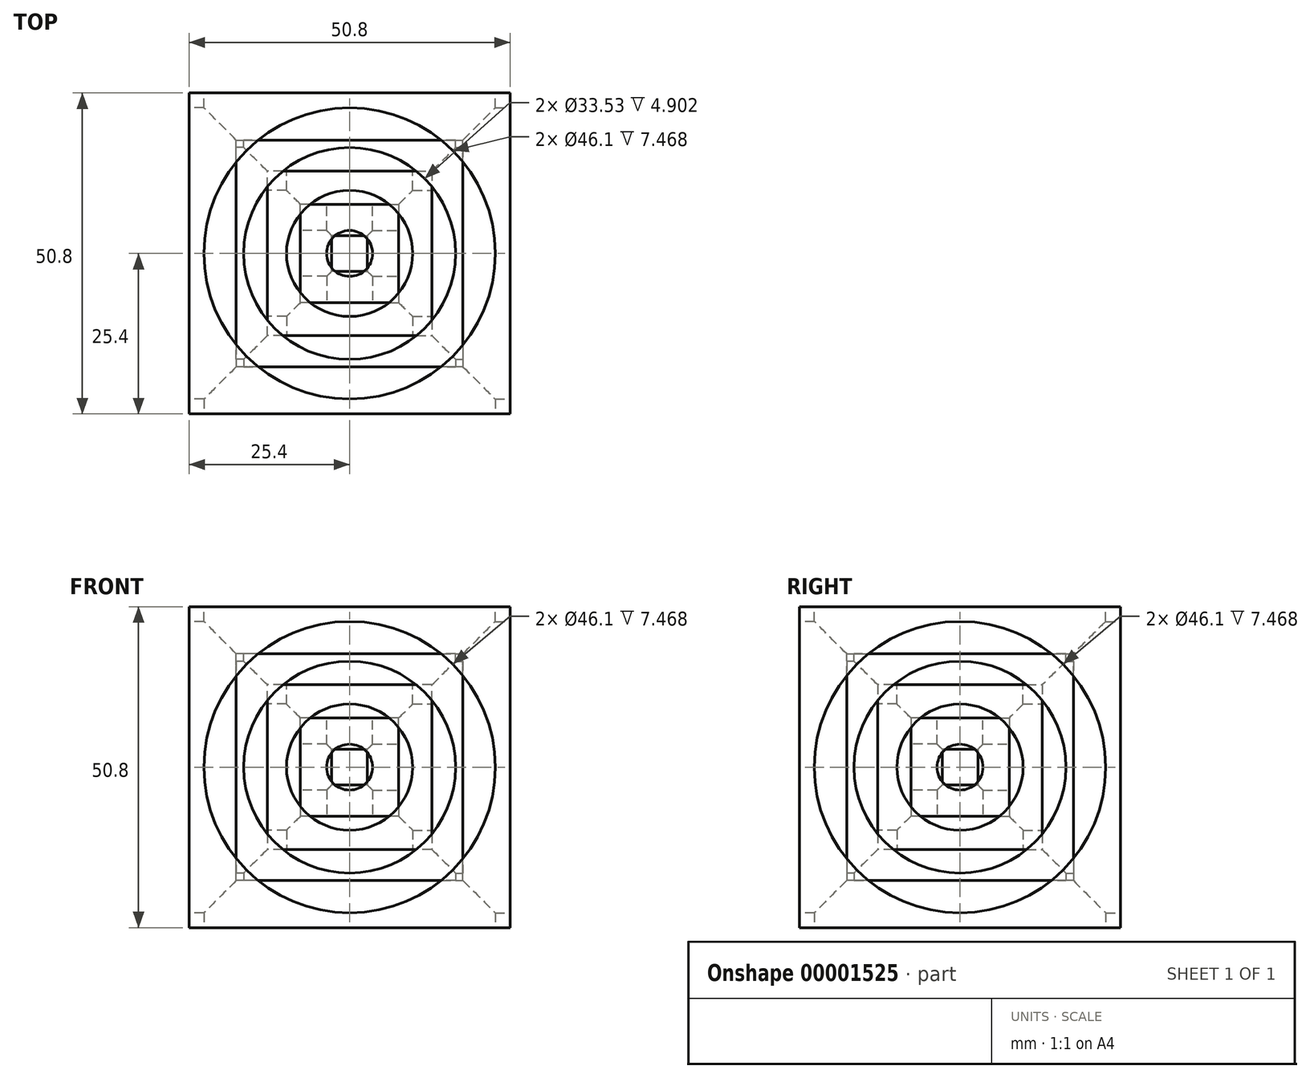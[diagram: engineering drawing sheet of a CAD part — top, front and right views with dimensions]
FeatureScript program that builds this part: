
annotation { "Feature Type Name" : "Feature", "Feature Type Description" : "" }
export const myFeature = defineFeature(function(context is Context, id is Id, definition is map)
    precondition{}
    {
        {
            var Q0;
            Q0=qCreatedBy(makeId("Top.planeOp"),FACE);
            var sketch = newSketch(context, id + "F0", { "sketchPlane" : qUnion([Q0])});
            skLineSegment(sketch, "E0.bottom", {"start": v(-25.4, 25.4) * mm, "end": v(25.4, 25.4) * mm});
            skLineSegment(sketch, "E0.top", {"start": v(-25.4, -25.4) * mm, "end": v(25.4, -25.4) * mm});
            skLineSegment(sketch, "E0.left", {"start": v(-25.4, 25.4) * mm, "end": v(-25.4, -25.4) * mm});
            skLineSegment(sketch, "E0.right", {"start": v(25.4, 25.4) * mm, "end": v(25.4, -25.4) * mm});
            skPoint(sketch, "E1", {"position": v(-25.4, 0) * mm});
            skPoint(sketch, "E2", {"position": v(0, 25.4) * mm});
            skSolve(sketch);
        }
        {
            var Q0;
            Q0 = qSketchRegion(id + "F0", true);
            extrude(context, id + "F1", {"entities" : qUnion([Q0]), "endBound" : BoundingType.SYMMETRIC, "oppositeDirection" : true, "depth" : 50.8 * mm});
        }
        {
            var Q0;
            Q0=qCreatedBy(makeId("Front.planeOp"),FACE);
            var sketch = newSketch(context, id + "F2", { "sketchPlane" : qUnion([Q0])});
            skLineSegment(sketch, "E3", {"start": v(23.05, 25.4) * mm, "end": v(23.05, 17.93) * mm});
            skLineSegment(sketch, "E4", {"start": v(23.05, 17.93) * mm, "end": v(16.76, 17.93) * mm});
            skLineSegment(sketch, "E5", {"start": v(16.76, 17.93) * mm, "end": v(16.76, 13.03) * mm});
            skLineSegment(sketch, "E6", {"start": v(16.76, 13.03) * mm, "end": v(9.98, 13.03) * mm});
            skLineSegment(sketch, "E7", {"start": v(9.98, 13.03) * mm, "end": v(9.98, 7.77) * mm});
            skLineSegment(sketch, "E8", {"start": v(9.98, 7.77) * mm, "end": v(3.63, 7.77) * mm});
            skLineSegment(sketch, "E9", {"start": v(3.63, 7.77) * mm, "end": v(3.63, 2.82) * mm});
            skLineSegment(sketch, "E10", {"start": v(3.63, 2.82) * mm, "end": v(0, 2.82) * mm});
            skLineSegment(sketch, "E11", {"start": v(0, 2.82) * mm, "end": v(0, 25.4) * mm});
            skLineSegment(sketch, "E12", {"start": v(0, 25.4) * mm, "end": v(23.05, 25.4) * mm});
            skLineSegment(sketch, "E13.0.MirrorCS", {"start": v(-23.05, 25.4) * mm, "end": v(-23.05, 17.93) * mm});
            skLineSegment(sketch, "E14.0.MirrorCS", {"start": v(-16.76, 17.93) * mm, "end": v(-16.76, 13.03) * mm});
            skLineSegment(sketch, "E15.0.MirrorCS", {"start": v(-9.98, 13.03) * mm, "end": v(-9.98, 7.77) * mm});
            skLineSegment(sketch, "E16.0.MirrorCS", {"start": v(-3.63, 7.77) * mm, "end": v(-3.63, 2.82) * mm});
            skLineSegment(sketch, "E17.0.MirrorCS", {"start": v(0, 25.4) * mm, "end": v(-23.05, 25.4) * mm});
            skLineSegment(sketch, "E18.0.MirrorCS", {"start": v(-23.05, 17.93) * mm, "end": v(-16.76, 17.93) * mm});
            skLineSegment(sketch, "E19.0.MirrorCS", {"start": v(-16.76, 13.03) * mm, "end": v(-9.98, 13.03) * mm});
            skLineSegment(sketch, "E20.0.MirrorCS", {"start": v(-9.98, 7.77) * mm, "end": v(-3.63, 7.77) * mm});
            skLineSegment(sketch, "E21.0.MirrorCS", {"start": v(-3.63, 2.82) * mm, "end": v(0, 2.82) * mm});
            skSolve(sketch);
        }
        {
            var Q0;
            Q0=makeQuery(id+"F2.imprint","IMPRINT",FACE,{"disambiguationData":[TD([[makeQuery(id+"F2.imprint","IMPRINT",EDGE,{"derivedFrom":sQuery(id+"F2.wireOp",EDGE,"E11")}),1.0]])]});
            var Q1;
            Q1=sQuery(id+"F2.wireOp",EDGE,"E11");
            revolve(context, id + "F3", {"operationType" : NewBodyOperationType.REMOVE, "entities" : qUnion([Q0]), "axis" : qUnion([Q1]), "revolveType" : RevolveType.FULL, "oppositeDirection" : true});
        }
        {
            var Q0;
            Q0=makeQuery(id+"F1.opExtrude","SWEPT_FACE",FACE,{"disambiguationData":[OSD([sQuery(id+"F0.wireOp",EDGE,"E0.top")])]});
            var sketch = newSketch(context, id + "F4", { "sketchPlane" : qUnion([Q0])});
            skLineSegment(sketch, "E22", {"start": v(25.4, 25.4) * mm, "end": v(25.4, -25.4) * mm});
            skLineSegment(sketch, "E23", {"start": v(-25.4, 25.4) * mm, "end": v(-25.4, -25.4) * mm});
            skLineSegment(sketch, "E24", {"start": v(-25.4, -25.4) * mm, "end": v(25.4, -25.4) * mm});
            skLineSegment(sketch, "E25", {"start": v(-25.4, 25.4) * mm, "end": v(0, 0) * mm});
            skLineSegment(sketch, "E26", {"start": v(0, 0) * mm, "end": v(25.4, 25.4) * mm});
            skSolve(sketch);
        }
        {
            var Q0;
            Q0=makeQuery(id+"F1.opExtrude","SWEPT_FACE",FACE,{"disambiguationData":[OSD([sQuery(id+"F0.wireOp",EDGE,"E0.right")])]});
            var sketch = newSketch(context, id + "F5", { "sketchPlane" : qUnion([Q0])});
            skLineSegment(sketch, "E27", {"start": v(25.4, 25.4) * mm, "end": v(25.4, -25.4) * mm});
            skLineSegment(sketch, "E28", {"start": v(25.4, -25.4) * mm, "end": v(-25.4, -25.4) * mm});
            skLineSegment(sketch, "E29", {"start": v(-25.4, -25.4) * mm, "end": v(-25.4, 25.4) * mm});
            skLineSegment(sketch, "E30", {"start": v(-25.4, 25.4) * mm, "end": v(0, 0) * mm});
            skLineSegment(sketch, "E31", {"start": v(0, 0) * mm, "end": v(25.4, 25.4) * mm});
            skSolve(sketch);
        }
        {
            var Q0;
            Q0 = qSketchRegion(id + "F4", true);
            extrude(context, id + "F6", {"entities" : qUnion([Q0]), "operationType" : NewBodyOperationType.REMOVE, "endBound" : BoundingType.THROUGH_ALL, "oppositeDirection" : true, "depth" : 25.4 * mm});
        }
        {
            var Q0;
            {var subQ6=sQuery(id+"F5.wireOp",EDGE,"E27");Q0=makeQuery(id+"F5.imprint","IMPRINT",FACE,{"disambiguationData":[TD([[makeQuery(id+"F5.imprint","IMPRINT",EDGE,{"derivedFrom":subQ6}),1.0]])]});}
            var Q1;
            {var subQ1=sQuery(id+"F5.wireOp",EDGE,"ec9ab9fc-b8ca-4a8f-b12b-c4621e4e10e5");var subQ3=sQuery(id+"F5.wireOp",EDGE,"824cf1f4-f9d0-47e6-97e3-05cd736923a9");var subQ5=makeQuery(id+"F5.imprint","INTERSECT",VERTEX,{"derivedFrom":[subQ3,subQ1]});Q1=makeQuery(id+"F5.imprint","IMPRINT",FACE,{"disambiguationData":[TD([[makeQuery(id+"F5.imprint","IMPRINT",EDGE,{"disambiguationData":[TD([[subQ5,1.0]])],"derivedFrom":subQ3}),-1.0]])]});}
            extrude(context, id + "F7", {"entities" : qUnion([Q0, Q1]), "operationType" : NewBodyOperationType.REMOVE, "endBound" : BoundingType.THROUGH_ALL, "oppositeDirection" : true, "depth" : 25.4 * mm});
        }
        {
            var Q0;
            Q0=makeQuery(id+"F1.opExtrude","SWEPT_BODY",BODY,{"disambiguationData":[OSD([sQuery(id+"F0.wireOp",EDGE,"E0.bottom"),sQuery(id+"F0.wireOp",EDGE,"E0.top"),sQuery(id+"F0.wireOp",EDGE,"E0.left"),sQuery(id+"F0.wireOp",EDGE,"E0.right")])]});
            var Q1;
            Q1=makeQuery(id+"F7.boolean.opBoolean","INTERSECT",EDGE,{"derivedFrom":[makeQuery(id+"F6.boolean.opBoolean","COPY",FACE,{"derivedFrom":makeQuery(id+"F6.opExtrude","SWEPT_FACE",FACE,{"disambiguationData":[OSD([sQuery(id+"F4.wireOp",EDGE,"E26")])]})}),makeQuery(id+"F7.opExtrude","SWEPT_FACE",FACE,{"disambiguationData":[OSD([sQuery(id+"F5.wireOp",EDGE,"E31")])]})]});
            transform(context, id + "F8", {"entities" : qUnion([Q0]), "transformType" : TransformType.ROTATION, "transformAxis" : qUnion([Q1]), "angle" : 120 * degree, "oppositeX" : false, "oppositeY" : false, "oppositeZ" : false, "makeCopy" : true});
        }
        {
            var Q0;
            Q0=makeQuery(id+"F8.opPattern","COPY",BODY,{"derivedFrom":makeQuery(id+"F1.opExtrude","SWEPT_BODY",BODY,{"disambiguationData":[OSD([sQuery(id+"F0.wireOp",EDGE,"E0.bottom"),sQuery(id+"F0.wireOp",EDGE,"E0.top"),sQuery(id+"F0.wireOp",EDGE,"E0.left"),sQuery(id+"F0.wireOp",EDGE,"E0.right")])]}),"instanceName":"1"});
            var Q1;
            Q1=makeQuery(id+"F1.opExtrude","SWEPT_BODY",BODY,{"disambiguationData":[OSD([sQuery(id+"F0.wireOp",EDGE,"E0.bottom"),sQuery(id+"F0.wireOp",EDGE,"E0.top"),sQuery(id+"F0.wireOp",EDGE,"E0.left"),sQuery(id+"F0.wireOp",EDGE,"E0.right")])]});
            var Q2;
            Q2=makeQuery(id+"F7.boolean.opBoolean","INTERSECT",EDGE,{"derivedFrom":[makeQuery(id+"F6.boolean.opBoolean","COPY",FACE,{"derivedFrom":makeQuery(id+"F6.opExtrude","SWEPT_FACE",FACE,{"disambiguationData":[OSD([sQuery(id+"F4.wireOp",EDGE,"d39d4b42-5a8d-42a1-9c56-47a1109cb90e")])]})}),makeQuery(id+"F7.opExtrude","SWEPT_FACE",FACE,{"disambiguationData":[OSD([sQuery(id+"F5.wireOp",EDGE,"824cf1f4-f9d0-47e6-97e3-05cd736923a9")])]})]});
            var Q3;
            Q3=makeQuery(id+"F7.boolean.opBoolean","INTERSECT",EDGE,{"derivedFrom":[makeQuery(id+"F6.boolean.opBoolean","COPY",FACE,{"derivedFrom":makeQuery(id+"F6.opExtrude","SWEPT_FACE",FACE,{"disambiguationData":[OSD([sQuery(id+"F4.wireOp",EDGE,"E25")])]})}),makeQuery(id+"F7.opExtrude","SWEPT_FACE",FACE,{"disambiguationData":[OSD([sQuery(id+"F5.wireOp",EDGE,"E31")])]})]});
            transform(context, id + "F9", {"entities" : qUnion([Q0, Q1]), "transformType" : TransformType.ROTATION, "transformAxis" : qUnion([Q3]), "angle" : 120 * degree, "oppositeX" : false, "oppositeY" : false, "oppositeZ" : false, "makeCopy" : true});
        }
        {
            var Q0;
            Q0=makeQuery(id+"F8.opPattern","COPY",BODY,{"derivedFrom":makeQuery(id+"F1.opExtrude","SWEPT_BODY",BODY,{"disambiguationData":[OSD([sQuery(id+"F0.wireOp",EDGE,"E0.bottom"),sQuery(id+"F0.wireOp",EDGE,"E0.top"),sQuery(id+"F0.wireOp",EDGE,"E0.left"),sQuery(id+"F0.wireOp",EDGE,"E0.right")])]}),"instanceName":"1"});
            var Q1;
            Q1=makeQuery(id+"F9.opPattern","COPY",BODY,{"derivedFrom":makeQuery(id+"F8.opPattern","COPY",BODY,{"derivedFrom":makeQuery(id+"F1.opExtrude","SWEPT_BODY",BODY,{"disambiguationData":[OSD([sQuery(id+"F0.wireOp",EDGE,"E0.bottom"),sQuery(id+"F0.wireOp",EDGE,"E0.top"),sQuery(id+"F0.wireOp",EDGE,"E0.left"),sQuery(id+"F0.wireOp",EDGE,"E0.right")])]}),"instanceName":"1"}),"instanceName":"1"});
            var Q2;
            Q2=makeQuery(id+"F7.boolean.opBoolean","INTERSECT",EDGE,{"derivedFrom":[makeQuery(id+"F6.boolean.opBoolean","COPY",FACE,{"derivedFrom":makeQuery(id+"F6.opExtrude","SWEPT_FACE",FACE,{"disambiguationData":[OSD([sQuery(id+"F4.wireOp",EDGE,"E26")])]})}),makeQuery(id+"F7.opExtrude","SWEPT_FACE",FACE,{"disambiguationData":[OSD([sQuery(id+"F5.wireOp",EDGE,"E31")])]})]});
            transform(context, id + "F10", {"entities" : qUnion([Q0, Q1]), "transformType" : TransformType.ROTATION, "transformAxis" : qUnion([Q2]), "angle" : 120 * degree, "oppositeX" : false, "oppositeY" : false, "oppositeZ" : false, "makeCopy" : true});
        }
        {
            var Q0;
            Q0=makeQuery(id+"F9.opPattern","COPY",BODY,{"derivedFrom":makeQuery(id+"F1.opExtrude","SWEPT_BODY",BODY,{"disambiguationData":[OSD([sQuery(id+"F0.wireOp",EDGE,"E0.bottom"),sQuery(id+"F0.wireOp",EDGE,"E0.top"),sQuery(id+"F0.wireOp",EDGE,"E0.left"),sQuery(id+"F0.wireOp",EDGE,"E0.right")])]}),"instanceName":"1"});
            var Q1;
            Q1=makeQuery(id+"F10.opPattern","COPY",BODY,{"derivedFrom":makeQuery(id+"F8.opPattern","COPY",BODY,{"derivedFrom":makeQuery(id+"F1.opExtrude","SWEPT_BODY",BODY,{"disambiguationData":[OSD([sQuery(id+"F0.wireOp",EDGE,"E0.bottom"),sQuery(id+"F0.wireOp",EDGE,"E0.top"),sQuery(id+"F0.wireOp",EDGE,"E0.left"),sQuery(id+"F0.wireOp",EDGE,"E0.right")])]}),"instanceName":"1"}),"instanceName":"1"});
            var Q2;
            Q2=makeQuery(id+"F1.opExtrude","SWEPT_BODY",BODY,{"disambiguationData":[OSD([sQuery(id+"F0.wireOp",EDGE,"E0.bottom"),sQuery(id+"F0.wireOp",EDGE,"E0.top"),sQuery(id+"F0.wireOp",EDGE,"E0.left"),sQuery(id+"F0.wireOp",EDGE,"E0.right")])]});
            var Q3;
            Q3=makeQuery(id+"F8.opPattern","COPY",BODY,{"derivedFrom":makeQuery(id+"F1.opExtrude","SWEPT_BODY",BODY,{"disambiguationData":[OSD([sQuery(id+"F0.wireOp",EDGE,"E0.bottom"),sQuery(id+"F0.wireOp",EDGE,"E0.top"),sQuery(id+"F0.wireOp",EDGE,"E0.left"),sQuery(id+"F0.wireOp",EDGE,"E0.right")])]}),"instanceName":"1"});
            var Q4;
            Q4=makeQuery(id+"F10.opPattern","COPY",BODY,{"derivedFrom":makeQuery(id+"F9.opPattern","COPY",BODY,{"derivedFrom":makeQuery(id+"F8.opPattern","COPY",BODY,{"derivedFrom":makeQuery(id+"F1.opExtrude","SWEPT_BODY",BODY,{"disambiguationData":[OSD([sQuery(id+"F0.wireOp",EDGE,"E0.bottom"),sQuery(id+"F0.wireOp",EDGE,"E0.top"),sQuery(id+"F0.wireOp",EDGE,"E0.left"),sQuery(id+"F0.wireOp",EDGE,"E0.right")])]}),"instanceName":"1"}),"instanceName":"1"}),"instanceName":"1"});
            var Q5;
            Q5=makeQuery(id+"F9.opPattern","COPY",BODY,{"derivedFrom":makeQuery(id+"F8.opPattern","COPY",BODY,{"derivedFrom":makeQuery(id+"F1.opExtrude","SWEPT_BODY",BODY,{"disambiguationData":[OSD([sQuery(id+"F0.wireOp",EDGE,"E0.bottom"),sQuery(id+"F0.wireOp",EDGE,"E0.top"),sQuery(id+"F0.wireOp",EDGE,"E0.left"),sQuery(id+"F0.wireOp",EDGE,"E0.right")])]}),"instanceName":"1"}),"instanceName":"1"});
            booleanBodies(context, id + "F11", {"operationType" : BooleanOperationType.UNION, "tools" : qUnion([Q0, Q1, Q2, Q3, Q4, Q5])});
        }
    });
